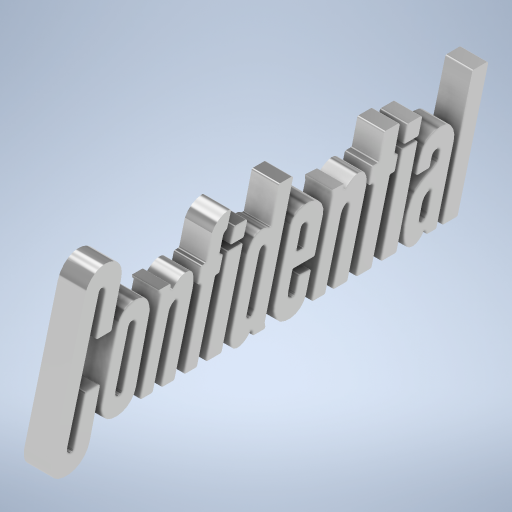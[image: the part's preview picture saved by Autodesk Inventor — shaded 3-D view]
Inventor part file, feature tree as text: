
AUTODESK INVENTOR PART (.ipt)
format: ipt  version: 2024 (Build 280153000, 153)  size: 817,152 bytes
history: native  units: in
note: dims shown in document units (in); Inventor stores cm internally (conversion verified against a paired STEP export)
features: other x2, sketch x2, extrude x2, plane x2
ambient origin geometry x8: Origin, YZ Plane, XZ Plane, XY Plane, X Axis, Y Axis, Z Axis, Center Point
bodies: Body1 (feature_tree)
feature tree (8):
  other  "Sólido1"
  sketch  "Boceto1"  dims[d5=0.025in d7=0.025in]
  extrude  "Extrusión1"  Depth=0.025in
  extrude  "Extrusión2"  Depth=0.025in
  plane  "Plano de trabajo1"
  plane  "Plano de trabajo2"
  sketch  "Boceto5"  dims[d8=0.025in d9=0.025in d10=0.025in d11=0.4in d12=0.0in d14=0.4in d15=0.0in d16=-111.375in d19=-31.125in d17=0.5in d18=0.0344in d20=0.0344in]
  other  "Imagen1"
